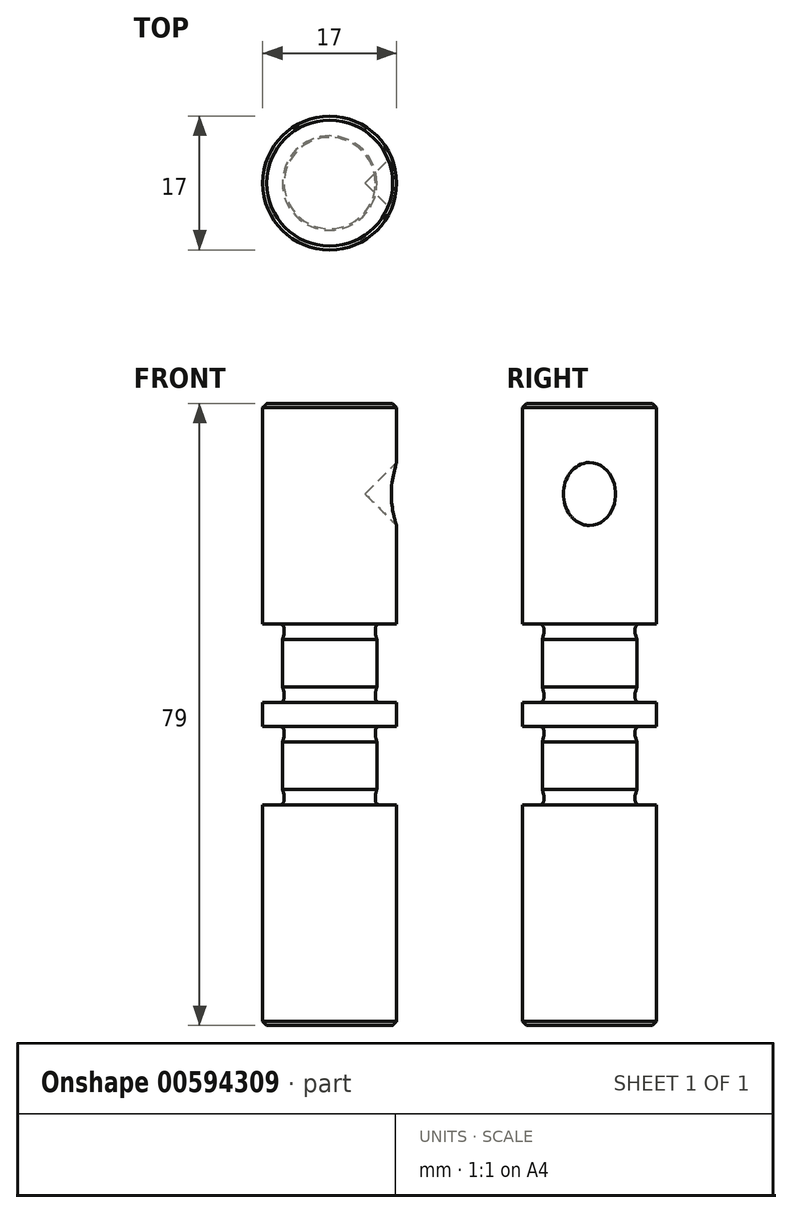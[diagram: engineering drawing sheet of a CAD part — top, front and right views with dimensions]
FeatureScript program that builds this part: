
annotation { "Feature Type Name" : "Feature", "Feature Type Description" : "" }
export const myFeature = defineFeature(function(context is Context, id is Id, definition is map)
    precondition{}
    {
        {
            var Q0;
            Q0=qCreatedBy(makeId("Front.planeOp"),FACE);
            var sketch = newSketch(context, id + "F0", { "sketchPlane" : qUnion([Q0])});
            skLineSegment(sketch, "E0", {"start": v(0, 0) * mm, "end": v(-8.5, 0) * mm});
            skLineSegment(sketch, "E1", {"start": v(-8.5, 0) * mm, "end": v(-8.5, 28) * mm});
            skLineSegment(sketch, "E2", {"start": v(-8.5, 28) * mm, "end": v(-6.4, 28) * mm});
            skLineSegment(sketch, "E3", {"start": v(-5.8, 28.6) * mm, "end": v(-5.8, 29.17) * mm});
            skLineSegment(sketch, "E4", {"start": v(-6, 30) * mm, "end": v(-6, 36) * mm});
            skLineSegment(sketch, "E5", {"start": v(-5.8, 36.83) * mm, "end": v(-5.8, 37.4) * mm});
            skLineSegment(sketch, "E6", {"start": v(-6.4, 38) * mm, "end": v(-8.5, 38) * mm});
            skLineSegment(sketch, "E7", {"start": v(-8.5, 38) * mm, "end": v(-8.5, 41) * mm});
            skLineSegment(sketch, "E8", {"start": v(-8.5, 41) * mm, "end": v(-6.4, 41) * mm});
            skLineSegment(sketch, "E9", {"start": v(-5.8, 41.6) * mm, "end": v(-5.8, 42.17) * mm});
            skLineSegment(sketch, "E10", {"start": v(-6, 43) * mm, "end": v(-6, 49) * mm});
            skLineSegment(sketch, "E11", {"start": v(-5.8, 49.83) * mm, "end": v(-5.8, 50.4) * mm});
            skLineSegment(sketch, "E12", {"start": v(-6.4, 51) * mm, "end": v(-8.5, 51) * mm});
            skLineSegment(sketch, "E13", {"start": v(-8.5, 51) * mm, "end": v(-8.5, 79) * mm});
            skLineSegment(sketch, "E14", {"start": v(-8.5, 79) * mm, "end": v(0, 79) * mm});
            skLineSegment(sketch, "E15", {"start": v(0, 79) * mm, "end": v(0, 0) * mm});
            skPoint(sketch, "E16.visualSharp", {"position": v(-5.8, 28) * mm});
            skArc(sketch, "E16.filletArc", {"start": v(-6.4, 28) * mm, "mid": v(-5.98, 28.18) * mm, "end": v(-5.8, 28.6) * mm});
            skLineSegment(sketch, "E17", {"start": v(-6, 30) * mm, "end": v(-5.82, 29.33) * mm});
            skLineSegment(sketch, "E18", {"start": v(-6, 36) * mm, "end": v(-5.82, 36.67) * mm});
            skPoint(sketch, "E19.visualSharp", {"position": v(-5.8, 29.25) * mm});
            skArc(sketch, "E19.filletArc", {"start": v(-5.8, 29.17) * mm, "mid": v(-5.8, 29.25) * mm, "end": v(-5.82, 29.33) * mm});
            skPoint(sketch, "E20.visualSharp", {"position": v(-5.8, 36.75) * mm});
            skArc(sketch, "E20.filletArc", {"start": v(-5.82, 36.67) * mm, "mid": v(-5.8, 36.75) * mm, "end": v(-5.8, 36.83) * mm});
            skPoint(sketch, "E21.visualSharp", {"position": v(-5.8, 38) * mm});
            skArc(sketch, "E21.filletArc", {"start": v(-5.8, 37.4) * mm, "mid": v(-5.98, 37.82) * mm, "end": v(-6.4, 38) * mm});
            skLineSegment(sketch, "E22", {"start": v(-6, 43) * mm, "end": v(-5.82, 42.33) * mm});
            skPoint(sketch, "E23.orphan", {"position": v(-5.8, 44.1) * mm});
            skPoint(sketch, "E24.visualSharp", {"position": v(-5.8, 42.25) * mm});
            skArc(sketch, "E24.filletArc", {"start": v(-5.8, 42.17) * mm, "mid": v(-5.8, 42.25) * mm, "end": v(-5.82, 42.33) * mm});
            skPoint(sketch, "E25.visualSharp", {"position": v(-5.8, 41) * mm});
            skArc(sketch, "E25.filletArc", {"start": v(-6.4, 41) * mm, "mid": v(-5.98, 41.18) * mm, "end": v(-5.8, 41.6) * mm});
            skLineSegment(sketch, "E26", {"start": v(-6, 49) * mm, "end": v(-5.82, 49.67) * mm});
            skPoint(sketch, "E27.end.orphan", {"position": v(-5.8, 48.5) * mm});
            skPoint(sketch, "E28.visualSharp", {"position": v(-5.8, 51) * mm});
            skArc(sketch, "E28.filletArc", {"start": v(-5.8, 50.4) * mm, "mid": v(-5.98, 50.82) * mm, "end": v(-6.4, 51) * mm});
            skPoint(sketch, "E29.visualSharp", {"position": v(-5.8, 49.75) * mm});
            skArc(sketch, "E29.filletArc", {"start": v(-5.82, 49.67) * mm, "mid": v(-5.8, 49.75) * mm, "end": v(-5.8, 49.83) * mm});
            skSolve(sketch);
        }
        {
            var Q0;
            Q0=makeQuery(id+"F0.imprint","IMPRINT",FACE,{"disambiguationData":[TD([[makeQuery(id+"F0.imprint","IMPRINT",EDGE,{"derivedFrom":sQuery(id+"F0.wireOp",EDGE,"E0")}),-1.0]])]});
            var Q1;
            Q1=sQuery(id+"F0.wireOp",EDGE,"E15");
            revolve(context, id + "F1", {"entities" : qUnion([Q0]), "axis" : qUnion([Q1]), "revolveType" : RevolveType.FULL});
        }
        {
            var Q0;
            Q0=qCreatedBy(makeId("Front.planeOp"),FACE);
            var sketch = newSketch(context, id + "F2", { "sketchPlane" : qUnion([Q0])});
            skLineSegment(sketch, "E30", {"start": v(-19.32, 67.5) * mm, "end": v(22.07, 67.5) * mm, "construction": true});
            skLineSegment(sketch, "E31", {"start": v(8.5, 79) * mm, "end": v(8.5, 51) * mm, "construction": true});
            skLineSegment(sketch, "E32", {"start": v(8.5, 71.5) * mm, "end": v(4.5, 67.5) * mm});
            skLineSegment(sketch, "E33", {"start": v(4.5, 67.5) * mm, "end": v(8.5, 67.5) * mm});
            skLineSegment(sketch, "E34", {"start": v(8.5, 67.5) * mm, "end": v(8.5, 71.5) * mm});
            skSolve(sketch);
        }
        {
            var Q0;
            Q0 = qSketchRegion(id + "F2", true);
            var Q1;
            Q1=sQuery(id+"F2.wireOp",EDGE,"E30");
            revolve(context, id + "F3", {"operationType" : NewBodyOperationType.REMOVE, "entities" : qUnion([Q0]), "axis" : qUnion([Q1]), "revolveType" : RevolveType.FULL, "oppositeDirection" : true});
        }
        {
            var Q0;
            Q0=makeQuery(id+"F1.opRevolve","SWEPT_EDGE",EDGE,{"disambiguationData":[OSD([sQuery(id+"F0.wireOp",EDGE,"E13"),sQuery(id+"F0.wireOp",EDGE,"E14")])]});
            var Q1;
            Q1=makeQuery(id+"F1.opRevolve","SWEPT_EDGE",EDGE,{"disambiguationData":[OSD([sQuery(id+"F0.wireOp",EDGE,"E0"),sQuery(id+"F0.wireOp",EDGE,"E1")])]});
            chamfer(context, id + "F4", {"entities" : qUnion([Q0, Q1]), "width" : .5 * mm, "tangentPropagation" : true});
        }
    });
